# Revit family: A02
name_source: partatom
category: Lighting Fixtures
revit_build: Autodesk Revit 2018 (Build: 20170223_1515(x64)
units: mm (PartAtom-declared; Revit-internal decimal feet)

## family parameters
Always vertical = Yes
Cut with Voids When Loaded = No
Host = Ceiling
Light Source = No
OmniClass Number = 23.80.70.11
OmniClass Title = Luminaries for Internal Lighting
Part Type = Normal
Room Calculation Point = No
Round Connector Dimension = Use Diameter
Shared = No

## types (9) — shared parameters
CRI = 92

## per-type parameters (varying)
| type | FINISH | Wattage Comments |
| A02-L1800-9TC-120V-92-30-P | P-WHITE | 120 |
| A02-L1800-9TC-120V-92-30-MB | MB-BLACK | 120 |
| A02-L1800-9TC-120V-92-30-CP | CP-CUSTOM FINISH | 120 |
| A02-L1800-9TC-240V-92-30-CP | CP-CUSTOM FINISH | 240 |
| A02-L1800-9TC-277V-92-30-CP | CP-CUSTOM FINISH | 277 |
| A02-L1800-9TC-240V-92-30-MB | MB-BLACK | 240 |
| A02-L1800-9TC-277V-92-30-MB | MB-BLACK | 277 |
| A02-L1800-9TC-240V-92-30-P | P-WHITE | 240 |
| A02-L1800-9TC-277V-92-30-P | P-WHITE | 277 |

## geometry (parser evidence)
native form markers: Sweep x9
no freeform markers — native parametric forms only
